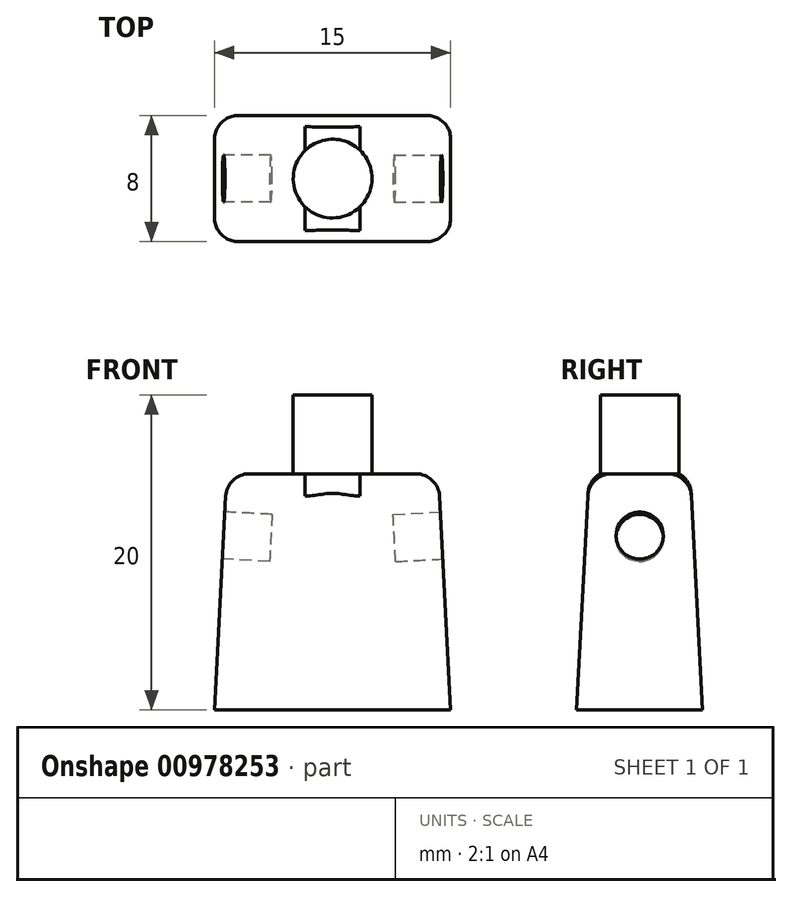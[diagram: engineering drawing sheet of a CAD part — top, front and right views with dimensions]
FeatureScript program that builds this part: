
annotation { "Feature Type Name" : "Feature", "Feature Type Description" : "" }
export const myFeature = defineFeature(function(context is Context, id is Id, definition is map)
    precondition{}
    {
        {
            var Q0;
            Q0=qCreatedBy(makeId("Top.planeOp"),FACE);
            var sketch = newSketch(context, id + "F0", { "sketchPlane" : qUnion([Q0])});
            skLineSegment(sketch, "E0.bottom", {"start": v(7.5, -4) * mm, "end": v(-7.5, -4) * mm});
            skLineSegment(sketch, "E0.top", {"start": v(7.5, 4) * mm, "end": v(-7.5, 4) * mm});
            skLineSegment(sketch, "E0.left", {"start": v(7.5, -4) * mm, "end": v(7.5, 4) * mm});
            skLineSegment(sketch, "E0.right", {"start": v(-7.5, -4) * mm, "end": v(-7.5, 4) * mm});
            skPoint(sketch, "E0.middle", {"position": v(0, 0) * mm});
            skSolve(sketch);
        }
        {
            var Q0;
            Q0=qSketchRegion(id+"F0",true);
            extrude(context, id + "F1", {"entities" : qUnion([Q0]), "depth" : 15 * mm, "offsetDistance" : 25.4 * mm, "hasDraft" : true, "draftAngle" : 3 * degree, "draftPullDirection" : true});
        }
        {
            var Q0;
            Q0=makeQuery(id+"F1.opExtrude","CAP_FACE",FACE,{"disambiguationData":[OSD([sQuery(id+"F0.wireOp",EDGE,"E0.bottom"),sQuery(id+"F0.wireOp",EDGE,"E0.top"),sQuery(id+"F0.wireOp",EDGE,"E0.left"),sQuery(id+"F0.wireOp",EDGE,"E0.right")])],"isStart":false});
            var sketch = newSketch(context, id + "F2", { "sketchPlane" : qUnion([Q0])});
            skCircle(sketch, "E1", {"center": v(0, 0) * mm, "radius": 2.5 * mm});
            skSolve(sketch);
        }
        {
            var Q0;
            Q0=makeQuery(id+"F2.imprint","IMPRINT",FACE,{"disambiguationData":[TD([[makeQuery(id+"F2.imprint","IMPRINT",EDGE,{"derivedFrom":sQuery(id+"F2.wireOp",EDGE,"E1")}),1.0]])]});
            extrude(context, id + "F3", {"entities" : qUnion([Q0]), "operationType" : NewBodyOperationType.ADD, "depth" : 5 * mm, "offsetDistance" : 25.4 * mm});
        }
        {
            var Q0;
            Q0=makeQuery(id+"F1.opExtrude","CAP_EDGE",EDGE,{"disambiguationData":[OSD([sQuery(id+"F0.wireOp",EDGE,"E0.top")])],"isStart":false});
            var Q1;
            Q1=makeQuery(id+"F1.opExtrude","CAP_EDGE",EDGE,{"disambiguationData":[OSD([sQuery(id+"F0.wireOp",EDGE,"E0.right")])],"isStart":false});
            var Q2;
            Q2=makeQuery(id+"F1.opExtrude","CAP_EDGE",EDGE,{"disambiguationData":[OSD([sQuery(id+"F0.wireOp",EDGE,"E0.bottom")])],"isStart":false});
            var Q3;
            Q3=makeQuery(id+"F1.opExtrude","CAP_EDGE",EDGE,{"disambiguationData":[OSD([sQuery(id+"F0.wireOp",EDGE,"E0.left")])],"isStart":false});
            var Q4;
            Q4=makeQuery(id+"F1.opExtrude","SWEPT_EDGE",EDGE,{"disambiguationData":[OSD([sQuery(id+"F0.wireOp",EDGE,"E0.top"),sQuery(id+"F0.wireOp",EDGE,"E0.left")])]});
            var Q5;
            Q5=makeQuery(id+"F1.opExtrude","SWEPT_EDGE",EDGE,{"disambiguationData":[OSD([sQuery(id+"F0.wireOp",EDGE,"E0.top"),sQuery(id+"F0.wireOp",EDGE,"E0.right")])]});
            var Q6;
            Q6=makeQuery(id+"F1.opExtrude","SWEPT_EDGE",EDGE,{"disambiguationData":[OSD([sQuery(id+"F0.wireOp",EDGE,"E0.bottom"),sQuery(id+"F0.wireOp",EDGE,"E0.right")])]});
            var Q7;
            Q7=makeQuery(id+"F1.opExtrude","SWEPT_EDGE",EDGE,{"disambiguationData":[OSD([sQuery(id+"F0.wireOp",EDGE,"E0.bottom"),sQuery(id+"F0.wireOp",EDGE,"E0.left")])]});
            fillet(context, id + "F4", {"entities" : qUnion([Q0, Q1, Q2, Q3, Q4, Q5, Q6, Q7]), "radius" : 1.5 * mm, "tangentPropagation" : true, "allowEdgeOverflow" : false});
        }
        {
            var Q0;
            Q0=makeQuery(id+"F1.opExtrude","SWEPT_FACE",FACE,{"disambiguationData":[OSD([sQuery(id+"F0.wireOp",EDGE,"E0.right")])]});
            var sketch = newSketch(context, id + "F5", { "sketchPlane" : qUnion([Q0])});
            skCircle(sketch, "E2", {"center": v(0, 10.7) * mm, "radius": 1.5 * mm});
            skSolve(sketch);
        }
        {
            var Q0;
            Q0=makeQuery(id+"F5.imprint","IMPRINT",FACE,{"disambiguationData":[TD([[makeQuery(id+"F5.imprint","IMPRINT",EDGE,{"derivedFrom":sQuery(id+"F5.wireOp",EDGE,"E2")}),1.0]])]});
            extrude(context, id + "F6", {"entities" : qUnion([Q0]), "operationType" : NewBodyOperationType.REMOVE, "oppositeDirection" : true, "depth" : 3 * mm, "offsetDistance" : 25.4 * mm});
        }
        {
            var Q0;
            Q0=makeQuery(id+"F1.opExtrude","SWEPT_FACE",FACE,{"disambiguationData":[OSD([sQuery(id+"F0.wireOp",EDGE,"E0.left")])]});
            var sketch = newSketch(context, id + "F7", { "sketchPlane" : qUnion([Q0])});
            skCircle(sketch, "E3", {"center": v(0, 10.7) * mm, "radius": 1.5 * mm});
            skSolve(sketch);
        }
        {
            var Q0;
            Q0=makeQuery(id+"F7.imprint","IMPRINT",FACE,{"disambiguationData":[TD([[makeQuery(id+"F7.imprint","IMPRINT",EDGE,{"derivedFrom":sQuery(id+"F7.wireOp",EDGE,"E3")}),1.0]])]});
            extrude(context, id + "F8", {"entities" : qUnion([Q0]), "operationType" : NewBodyOperationType.REMOVE, "oppositeDirection" : true, "depth" : 3 * mm, "offsetDistance" : 25.4 * mm});
        }
    });
